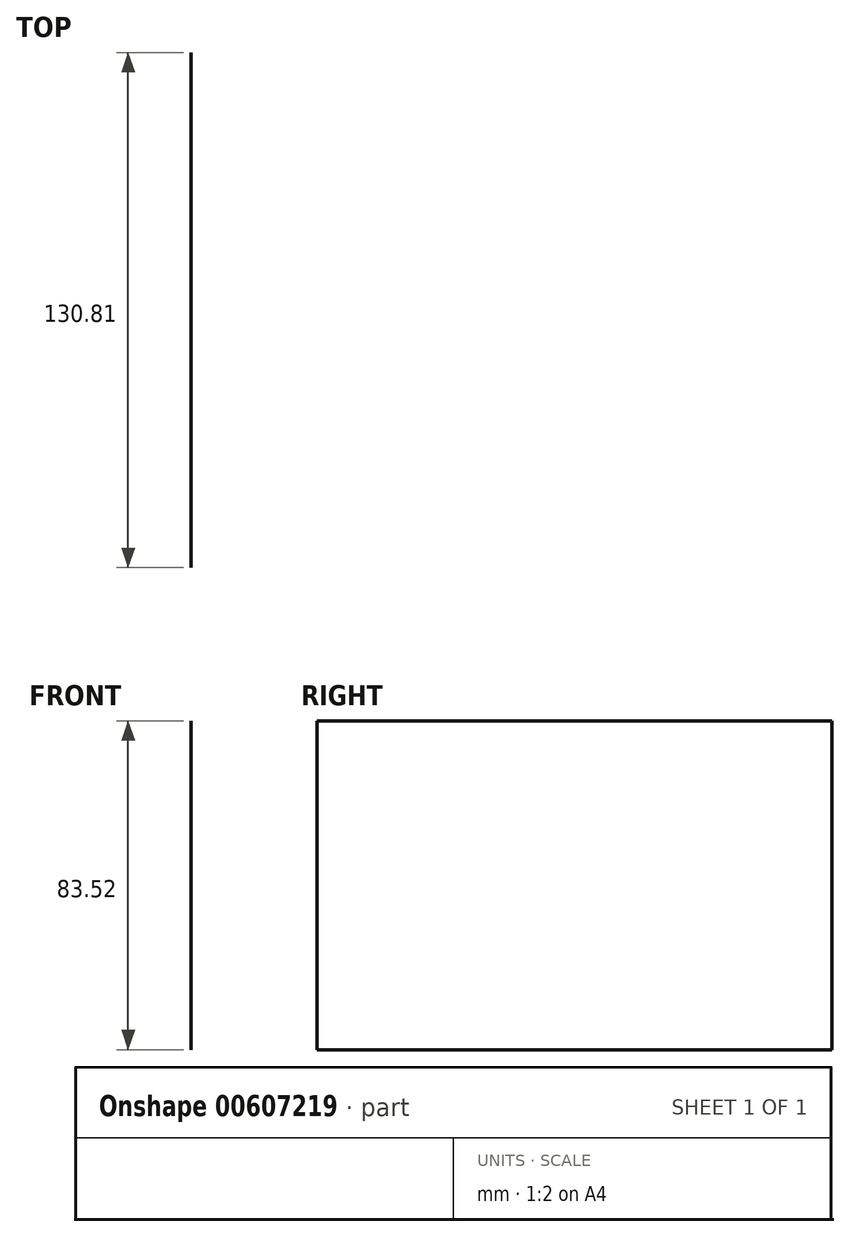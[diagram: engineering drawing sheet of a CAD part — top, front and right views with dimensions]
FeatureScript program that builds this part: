
annotation { "Feature Type Name" : "Feature", "Feature Type Description" : "" }
export const myFeature = defineFeature(function(context is Context, id is Id, definition is map)
    precondition{}
    {
        {
            var Q0;
            Q0=qCreatedBy(makeId("Front.planeOp"),FACE);
            var sketch = newSketch(context, id + "F0", { "sketchPlane" : qUnion([Q0])});
            skLineSegment(sketch, "E0", {"start": v(0, 0) * mm, "end": v(0, 83.52) * mm});
            skSolve(sketch);
        }
        {
            var Q0;
            Q0=sQuery(id+"F0.wireOp",EDGE,"E0");
            extrude(context, id + "F1", {"bodyType" : ToolBodyType.SURFACE, "surfaceEntities" : qUnion([Q0]), "oppositeDirection" : true, "depth" : 130.8 * mm, "offsetDistance" : 25.4 * mm});
        }
    });
